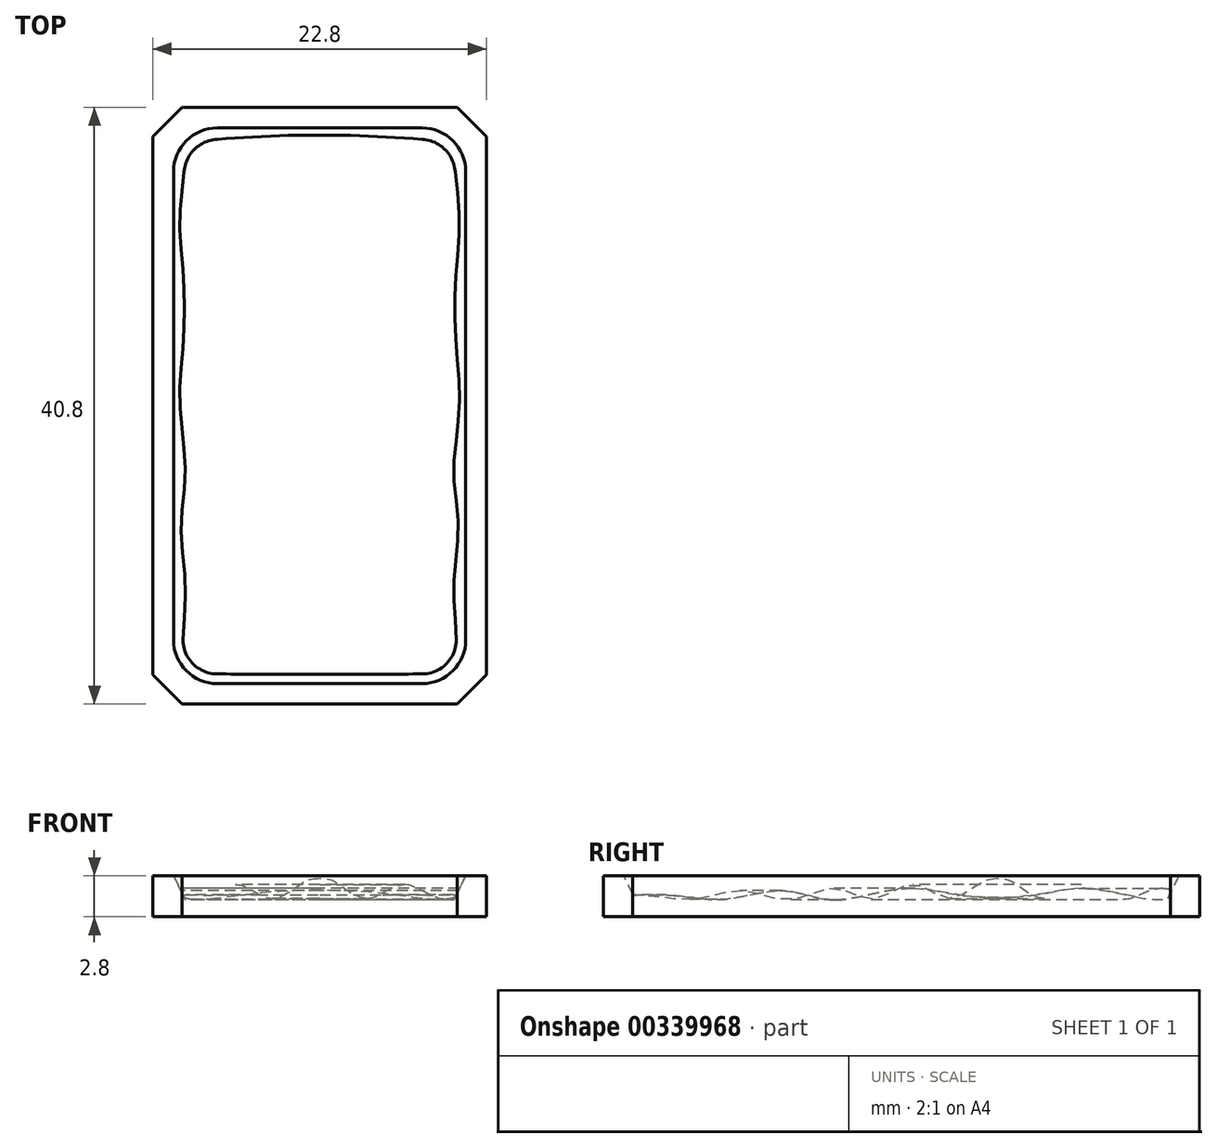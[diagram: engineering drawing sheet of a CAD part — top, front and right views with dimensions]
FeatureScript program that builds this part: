
annotation { "Feature Type Name" : "Feature", "Feature Type Description" : "" }
export const myFeature = defineFeature(function(context is Context, id is Id, definition is map)
    precondition{}
    {
        {
            var Q0;
            Q0=qCreatedBy(makeId("Top.planeOp"),FACE);
            var sketch = newSketch(context, id + "F0", { "sketchPlane" : qUnion([Q0])});
            skLineSegment(sketch, "E0.bottom", {"start": v(-9, 18) * mm, "end": v(9, 18) * mm});
            skLineSegment(sketch, "E0.top", {"start": v(-9, -18) * mm, "end": v(9, -18) * mm});
            skLineSegment(sketch, "E0.left", {"start": v(-9, 18) * mm, "end": v(-9, -18) * mm});
            skLineSegment(sketch, "E0.right", {"start": v(9, 18) * mm, "end": v(9, -18) * mm});
            skPoint(sketch, "E0.middle", {"position": v(0, 0) * mm});
            skSolve(sketch);
        }
        {
            var Q0;
            Q0 = qSketchRegion(id + "F0", true);
            extrude(context, id + "F1", {"entities" : qUnion([Q0]), "depth" : 1 * mm, "offsetDistance" : 25 * mm});
        }
        {
            var Q0;
            Q0=qCreatedBy(makeId("Right.planeOp"),FACE);
            var sketch = newSketch(context, id + "F2", { "sketchPlane" : qUnion([Q0])});
            skLineSegment(sketch, "E1.0", {"start": v(18, 1) * mm, "end": v(-18, 1) * mm});
            skLineSegment(sketch, "E2", {"start": v(6.55, 1) * mm, "end": v(6.55, 2.6) * mm});
            skFitSpline(sketch, "E3", {"points": [v(6.55, 2.6) * mm, v(5.25, 2.2) * mm, v(3.22, 1.26) * mm, v(0.82, 2.2) * mm, v(-1.96, 1.2) * mm, v(-4.5, 1.94) * mm, v(-7.65, 1.15) * mm, v(-10.88, 1.78) * mm, v(-14.17, 1.2) * mm, v(-18.28, 1.5) * mm, v(-24.69, 1.22) * mm, v(-28.35, 1.73) * mm, v(-31.52, 1) * mm], "startDerivative": vector(-34.56, 0.08) * mm, "endDerivative": vector(-36.53, -9.66) * mm});
            skLineSegment(sketch, "E4", {"start": v(-18, 1) * mm, "end": v(-31.52, 1) * mm});
            skSolve(sketch);
        }
        {
            var Q0;
            Q0 = qSketchRegion(id + "F2", true);
            var Q1;
            Q1=sQuery(id+"F2.wireOp",EDGE,"E2");
            revolve(context, id + "F3", {"operationType" : NewBodyOperationType.ADD, "entities" : qUnion([Q0]), "axis" : qUnion([Q1]), "revolveType" : RevolveType.FULL});
        }
        {
            var Q0;
            Q0=makeQuery(id+"F3.opRevolve","SWEPT_FACE",FACE,{"disambiguationData":[OSD([sQuery(id+"F2.wireOp",EDGE,"E1.0"),sQuery(id+"F2.wireOp",EDGE,"E4")])]});
            extrude(context, id + "F4", {"entities" : qUnion([Q0]), "operationType" : NewBodyOperationType.REMOVE, "oppositeDirection" : true, "depth" : 25 * mm, "offsetDistance" : 25 * mm});
        }
        {
            var Q0;
            {var subQ0=sQuery(id+"F0.wireOp",EDGE,"E0.left");var subQ1=sQuery(id+"F0.wireOp",EDGE,"E0.bottom");Q0=makeQuery(id+"F4.boolean.opBoolean","MERGE",EDGE,{"derivedFrom":[makeQuery(id+"F1.opExtrude","SWEPT_EDGE",EDGE,{"disambiguationData":[OSD([subQ1,subQ0])]}),makeQuery(id+"F4.opExtrude","SWEPT_EDGE",EDGE,{"disambiguationData":[OSD([subQ1,subQ0])]})]});}
            var Q1;
            {var subQ0=sQuery(id+"F0.wireOp",EDGE,"E0.right");var subQ1=sQuery(id+"F0.wireOp",EDGE,"E0.bottom");Q1=makeQuery(id+"F4.boolean.opBoolean","MERGE",EDGE,{"derivedFrom":[makeQuery(id+"F1.opExtrude","SWEPT_EDGE",EDGE,{"disambiguationData":[OSD([subQ1,subQ0])]}),makeQuery(id+"F4.opExtrude","SWEPT_EDGE",EDGE,{"disambiguationData":[OSD([subQ1,subQ0])]})]});}
            var Q2;
            {var subQ0=sQuery(id+"F0.wireOp",EDGE,"E0.left");var subQ1=sQuery(id+"F0.wireOp",EDGE,"E0.top");Q2=makeQuery(id+"F4.boolean.opBoolean","MERGE",EDGE,{"derivedFrom":[makeQuery(id+"F1.opExtrude","SWEPT_EDGE",EDGE,{"disambiguationData":[OSD([subQ1,subQ0])]}),makeQuery(id+"F4.opExtrude","SWEPT_EDGE",EDGE,{"disambiguationData":[OSD([subQ1,subQ0])]})]});}
            var Q3;
            {var subQ0=sQuery(id+"F0.wireOp",EDGE,"E0.right");var subQ1=sQuery(id+"F0.wireOp",EDGE,"E0.top");Q3=makeQuery(id+"F4.boolean.opBoolean","MERGE",EDGE,{"derivedFrom":[makeQuery(id+"F1.opExtrude","SWEPT_EDGE",EDGE,{"disambiguationData":[OSD([subQ1,subQ0])]}),makeQuery(id+"F4.opExtrude","SWEPT_EDGE",EDGE,{"disambiguationData":[OSD([subQ1,subQ0])]})]});}
            fillet(context, id + "F5", {"entities" : qUnion([Q0, Q1, Q2, Q3]), "radius" : 2 * mm, "tangentPropagation" : true, "allowEdgeOverflow" : false});
        }
        {
            var Q0;
            Q0=makeQuery(id+"F1.opExtrude","CAP_FACE",FACE,{"disambiguationData":[OSD([sQuery(id+"F0.wireOp",EDGE,"E0.bottom"),sQuery(id+"F0.wireOp",EDGE,"E0.top"),sQuery(id+"F0.wireOp",EDGE,"E0.left"),sQuery(id+"F0.wireOp",EDGE,"E0.right")])],"isStart":true});
            var sketch = newSketch(context, id + "F6", { "sketchPlane" : qUnion([Q0])});
            skArc(sketch, "E5.0", {"start": v(11.4, 16) * mm, "mid": v(10.11, 19.11) * mm, "end": v(7, 20.4) * mm});
            skLineSegment(sketch, "E5.1", {"start": v(11.4, -16) * mm, "end": v(11.4, 16) * mm});
            skLineSegment(sketch, "E5.2", {"start": v(7, 20.4) * mm, "end": v(-7, 20.4) * mm});
            skArc(sketch, "E5.3", {"start": v(7, -20.4) * mm, "mid": v(10.11, -19.11) * mm, "end": v(11.4, -16) * mm});
            skArc(sketch, "E5.4", {"start": v(-7, 20.4) * mm, "mid": v(-10.11, 19.11) * mm, "end": v(-11.4, 16) * mm});
            skLineSegment(sketch, "E5.5", {"start": v(-11.4, 16) * mm, "end": v(-11.4, -16) * mm});
            skArc(sketch, "E5.6", {"start": v(-11.4, -16) * mm, "mid": v(-10.11, -19.11) * mm, "end": v(-7, -20.4) * mm});
            skLineSegment(sketch, "E5.7", {"start": v(-7, -20.4) * mm, "end": v(7, -20.4) * mm});
            skLineSegment(sketch, "E6.bottom", {"start": v(-11.4, 20.4) * mm, "end": v(11.4, 20.4) * mm});
            skLineSegment(sketch, "E6.top", {"start": v(-11.4, -20.4) * mm, "end": v(11.4, -20.4) * mm});
            skLineSegment(sketch, "E6.left", {"start": v(-11.4, 20.4) * mm, "end": v(-11.4, -20.4) * mm});
            skLineSegment(sketch, "E6.right", {"start": v(11.4, 20.4) * mm, "end": v(11.4, -20.4) * mm});
            skPoint(sketch, "E6.middle", {"position": v(0, 0) * mm});
            skSolve(sketch);
        }
        {
            var Q0;
            {var subQ0=sQuery(id+"F6.wireOp",EDGE,"E5.0");Q0=makeQuery(id+"F6.imprint","IMPRINT",FACE,{"disambiguationData":[TD([[makeQuery(id+"F6.imprint","IMPRINT",EDGE,{"derivedFrom":subQ0}),-1.0]])]});}
            var Q1;
            {var subQ0=sQuery(id+"F6.wireOp",EDGE,"E5.3");Q1=makeQuery(id+"F6.imprint","IMPRINT",FACE,{"disambiguationData":[TD([[makeQuery(id+"F6.imprint","IMPRINT",EDGE,{"derivedFrom":subQ0}),-1.0]])]});}
            var Q2;
            {var subQ0=sQuery(id+"F6.wireOp",EDGE,"E5.4");Q2=makeQuery(id+"F6.imprint","IMPRINT",FACE,{"disambiguationData":[TD([[makeQuery(id+"F6.imprint","IMPRINT",EDGE,{"derivedFrom":subQ0}),-1.0]])]});}
            var Q3;
            {var subQ0=sQuery(id+"F6.wireOp",EDGE,"E5.6");Q3=makeQuery(id+"F6.imprint","IMPRINT",FACE,{"disambiguationData":[TD([[makeQuery(id+"F6.imprint","IMPRINT",EDGE,{"derivedFrom":subQ0}),-1.0]])]});}
            var Q4;
            {var subQ6=sQuery(id+"F6.wireOp",EDGE,"E5.0");Q4=makeQuery(id+"F6.imprint","IMPRINT",FACE,{"disambiguationData":[TD([[makeQuery(id+"F6.imprint","IMPRINT",EDGE,{"derivedFrom":subQ6}),1.0]])]});}
            extrude(context, id + "F7", {"entities" : qUnion([Q0, Q1, Q2, Q3, Q4]), "operationType" : NewBodyOperationType.ADD, "oppositeDirection" : true, "depth" : 2.8 * mm, "offsetDistance" : 25 * mm});
        }
        {
            var Q0;
            Q0=makeQuery(id+"F7.opExtrude","CAP_EDGE",EDGE,{"disambiguationData":[OSD([sQuery(id+"F0.wireOp",EDGE,"E0.left")])],"isStart":false});
            chamfer(context, id + "F8", {"entities" : qUnion([Q0]), "chamferType" : ChamferType.TWO_OFFSETS, "width1" : 2 * mm, "oppositeDirection" : false, "width2" : 1 * mm, "tangentPropagation" : true});
        }
        {
            var Q0;
            Q0=makeQuery(id+"F7.opExtrude","SWEPT_EDGE",EDGE,{"disambiguationData":[OSD([sQuery(id+"F6.wireOp",EDGE,"E6.top"),sQuery(id+"F6.wireOp",EDGE,"E6.left")])]});
            var Q1;
            Q1=makeQuery(id+"F7.opExtrude","SWEPT_EDGE",EDGE,{"disambiguationData":[OSD([sQuery(id+"F6.wireOp",EDGE,"E6.top"),sQuery(id+"F6.wireOp",EDGE,"E6.right")])]});
            var Q2;
            Q2=makeQuery(id+"F7.opExtrude","SWEPT_EDGE",EDGE,{"disambiguationData":[OSD([sQuery(id+"F6.wireOp",EDGE,"E6.bottom"),sQuery(id+"F6.wireOp",EDGE,"E6.left")])]});
            var Q3;
            Q3=makeQuery(id+"F7.opExtrude","SWEPT_EDGE",EDGE,{"disambiguationData":[OSD([sQuery(id+"F6.wireOp",EDGE,"E6.bottom"),sQuery(id+"F6.wireOp",EDGE,"E6.right")])]});
            chamfer(context, id + "F9", {"entities" : qUnion([Q0, Q1, Q2, Q3]), "width" : 2 * mm, "tangentPropagation" : true});
        }
    });
